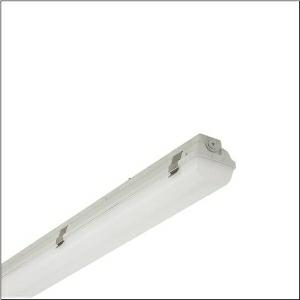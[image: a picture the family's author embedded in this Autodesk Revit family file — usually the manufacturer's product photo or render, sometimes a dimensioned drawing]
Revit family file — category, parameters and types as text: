
# Revit family: monsun_21_eco_51fj20dl45a
name_source: partatom
category: Lighting Fixtures
units: mm (PartAtom-declared; Revit-internal decimal feet)

## family parameters
Cut with Voids When Loaded = No
Host = Face
Light Source = No
Part Type = Normal
Room Calculation Point = No
Round Connector Dimension = Use Diameter
Shared = No

## types (1)
- Monsun 21 Eco (1 x LED, 4900 lm, 36 W, 4000K)
    Apparent Load = 36 VA
    CIE Flux Codes = 40 69 88 88 100
    Color Rendering = 80
    Color Temperature = 4000K
    Default Elevation = 1800 mm
    Description = Monsun 21 Eco, damp-proof luminaire, primary optical cover: diffuser, of PC, UV-stabilised, frosted, light emission: direct distribution, primary light characteristic: symmetric, installation type: suspended mounting, surface-mounted, LED, rated luminous flux: 4.900lm, luminous efficacy: 132lm/W, light colour: 840, colour temperature: 4000K, control gear: DALI, with terminal, 5-pole, max. 2.5mm², mains connection: 220..240V, AC, 50/60Hz, rated input power: 36W, housing, of glass-fibre reinforced polyester, light grey (RAL 7035), length: 1.277mm, width: 90mm, height: 95mm, clip for enclosure, of spring steel V2A, protection rating (complete): IP66, insulation class (complete): insulation class I (protective earthing), certification: CE, UKCA, protection symbol: D, impact resistance: IK08, permissible operating ambient temperature: -20..+35°C, corresponds to IFS (International Featured Standards) requirements for safety and quality in the food industry, contact your sales advisor before using the luminaires in applications with unclear chemical exposure, large temperature fluctuations or condensation-forming humidity, packaging unit: 1 piece
    Height = 103 mm
    Lamp = 1 x LED
    Lamp Light Flux = 4900 lm
    Lamp Power = 36 W
    Lamp count = 1
    Length = 1277 mm
    Luminous efficacy = 136 lm/W
    Manufacturer = Siteco
    ModVariant = No
    Model = 51FJ20DL45A
    Mounting Place = Ceiling
    Mounting Type = Surface mounted
    Number of Poles = 1
    OnlyDefault = Yes
    Power Factor = 1
    Product Name = Monsun 21 Eco
    Product group = damp-proof luminaire
    ProductGroupID = 300
    Protection Class = Protection class I
    Protection Degree = IP 66
    RLX_Detail_Level = 1
    RLX_Emergency_Light_Flux = 0 lm
    RLX_Emergency_Type = 0
    RLX_Emergency_Type_DB = No
    RlxData = <blob elided: 33333 chars, md5=a26abc03>
    Socket = socket
    Standby Power = 0 W
    System Light Flux = 4900 lm
    System Power = 36 W
    Type Comments = Product without accessories
    Type Image = l_1007218.jpg
    URL = http://relux.com
    VarID = ---
    Voltage = 0 V
    Weight = 0.00 kg
    Width = 90 mm

## geometry (parser evidence)
native form markers: Blend x4, Sweep x12
no freeform markers — native parametric forms only
